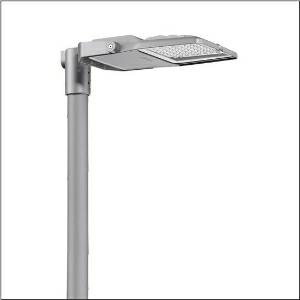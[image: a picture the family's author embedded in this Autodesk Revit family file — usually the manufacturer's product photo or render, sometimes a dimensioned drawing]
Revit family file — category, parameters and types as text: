
# Revit family: floodlight_fl_21_iq_mini___pl43_5xa7772c2a3a_c494
name_source: partatom
category: Lighting Fixtures
units: mm (PartAtom-declared; Revit-internal decimal feet)

## family parameters
Cut with Voids When Loaded = No
Host = Face
Light Source = No
Part Type = Normal
Room Calculation Point = No
Round Connector Dimension = Use Diameter
Shared = No

## types (1)
- --- (1 x LED, 12520 lm, 87.2 W, 3000K)
    Apparent Load = 87 VA
    CIE Flux Codes = 27 78 99 100 100
    Color Rendering = 70
    Color Temperature = 3000K
    Default Elevation = 1800 mm
    Description = Floodlight FL 21 iQ mini, floodlight, primary light control with lens, of PMMA, primary optical cover: protective disc, of toughened safety glass, transparent, light distribution: PL43, light emission: direct distribution, installation type: surface-mounted, LED, High Power LED, rated luminous flux: 12.520lm, luminous efficacy: 144lm/W, light colour: 730, colour temperature: 3000K, control gear: iQ Street-Remote/DALI, control: Auto-Match, Temp-Guard, Night-Set, Smart-Wire, Desk-Remote (wireless, voltage-free reading and setting of iQ features in the workshop via application-optimized NFC function/RFID function), optimised constant luminous flux control (CLO 2.0), Light-Fading, Lumen-Switch, with terminal, 6-pole, mains connection: 220..240V, AC, 50/60Hz, start of lifetime: 87W, end of service life: 92W, reduction: 40W, luminaire housing, of diecast aluminium, powder-coated, Siteco® metallic grey (DB 702S), corrosivity category C5 mid according to DIN EN ISO 12944, suitable for swimming pools, chlorine-resistant, sealing non-destructively replaceable, please order mast flange separately, mast bracket, of steel, galvanised, powder-coated, protection rating (complete): IP66, insulation class (complete): insulation class II (safety insulation), certification: CE, ENEC, VDE, protection symbol: D, impact resistance: IK08, permissible operating ambient temperature: -40..+40°C, permissible operating ambient temperature for outdoor applications: -40..+50°C, standard: DIN EN 12944, LABS conformity tested according to VDMA 24364:2018-05, packaging unit: 1 piece

Light Distribution: PL43
    Height = 70 mm
    Lamp = 1 x LED
    Lamp Light Flux = 12520 lm
    Lamp Power = 87.2 W
    Lamp count = 1
    Length = 485 mm
    Luminous efficacy = 144 lm/W
    Manufacturer = Siteco
    ModVariant = No
    Model = 5XA7772C2A3A
    Number of Poles = 1
    OnlyDefault = Yes
    Power Factor = 1
    Product Name = Floodlight FL 21 iQ mini | PL43
    Product group = floodlight | pylon annexe
    ProductGroupID = 6200
    Protection Class = Protection class II
    Protection Degree = IP 66
    RLX_Detail_Level = 1
    RLX_Emergency_Light_Flux = 0 lm
    RLX_Emergency_Type = 0
    RLX_Emergency_Type_DB = No
    RlxData = <blob elided: 101365 chars, md5=cd9e9048>
    Socket = socket
    Standby Power = 0 W
    System Light Flux = 12520 lm
    System Power = 87 W
    Type Comments = factory setting: luminous flux: 100 % | dim-lin: 254 | 456 mA
    Type Image = l_1007125.jpg
    URL = http://relux.com
    VarID = @adj_162306
    Voltage = 0 V
    Weight = 0.00 kg
    Width = 337 mm

## geometry (parser evidence)
native form markers: Blend x4, Sweep x11
no freeform markers — native parametric forms only
